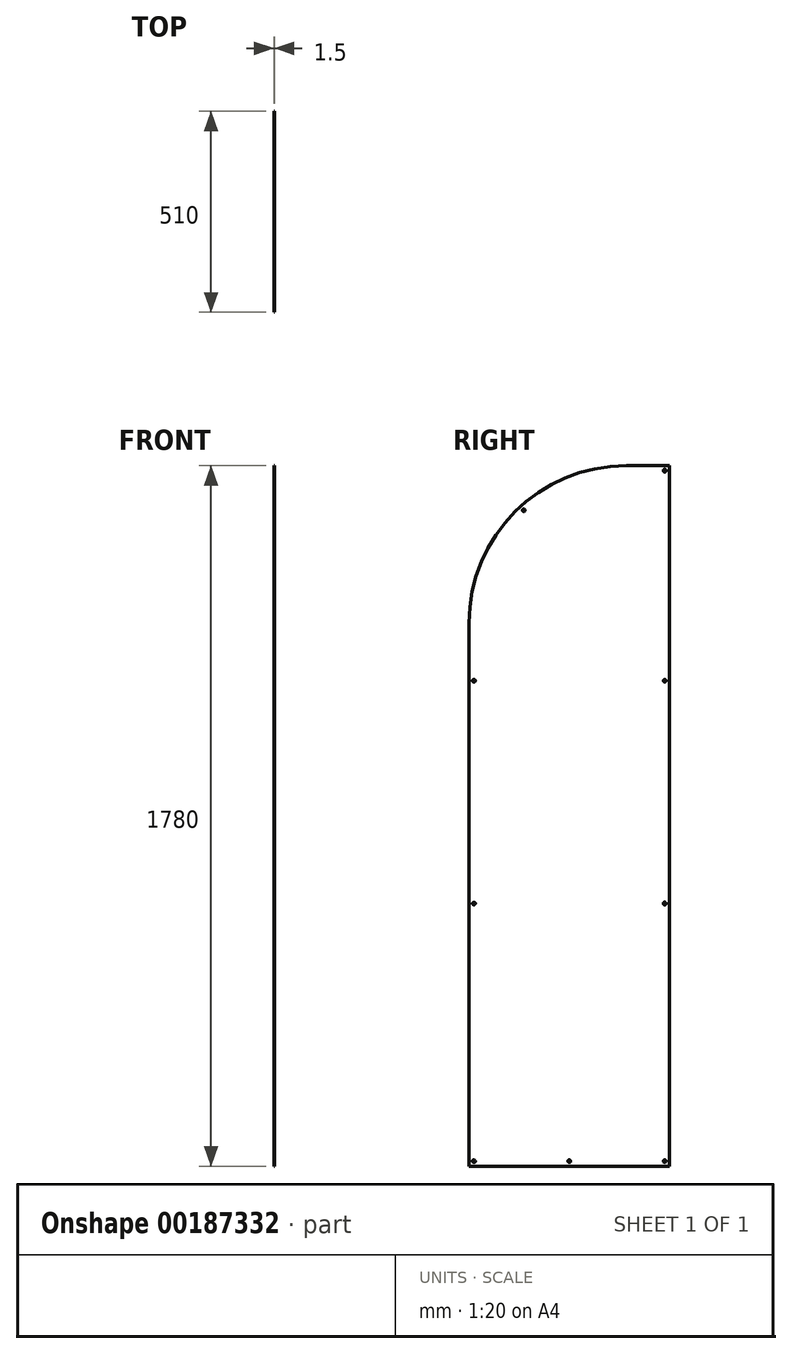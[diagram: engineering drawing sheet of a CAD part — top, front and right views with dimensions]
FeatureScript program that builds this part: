
annotation { "Feature Type Name" : "Feature", "Feature Type Description" : "" }
export const myFeature = defineFeature(function(context is Context, id is Id, definition is map)
    precondition{}
    {
        {
            var Q0;
            Q0=qCreatedBy(makeId("Right.planeOp"),FACE);
            var sketch = newSketch(context, id + "F0", { "sketchPlane" : qUnion([Q0])});
            skLineSegment(sketch, "E0.bottom", {"start": v(255, 890) * mm, "end": v(145, 890) * mm});
            skLineSegment(sketch, "E0.top", {"start": v(255, -890) * mm, "end": v(-255, -890) * mm});
            skLineSegment(sketch, "E0.left", {"start": v(255, 890) * mm, "end": v(255, -890) * mm});
            skLineSegment(sketch, "E0.right", {"start": v(-255, 490) * mm, "end": v(-255, -890) * mm});
            skPoint(sketch, "E0.middle", {"position": v(0, 0) * mm});
            skPoint(sketch, "E1.visualSharp", {"position": v(-255, 890) * mm});
            skArc(sketch, "E1.filletArc", {"start": v(145, 890) * mm, "mid": v(-137.84, 772.84) * mm, "end": v(-255, 490) * mm});
            skCircle(sketch, "E2", {"center": v(0, -877.3) * mm, "radius": 3.5 * mm});
            skCircle(sketch, "E3", {"center": v(-242.3, -877.3) * mm, "radius": 3.5 * mm});
            skCircle(sketch, "E4", {"center": v(242.3, -877.3) * mm, "radius": 3.5 * mm});
            skCircle(sketch, "E5", {"center": v(242.3, -222.65) * mm, "radius": 3.5 * mm});
            skCircle(sketch, "E6", {"center": v(-242.3, -222.65) * mm, "radius": 3.5 * mm});
            skCircle(sketch, "E7", {"center": v(242.3, 343.45) * mm, "radius": 3.5 * mm});
            skCircle(sketch, "E8", {"center": v(-242.3, 343.45) * mm, "radius": 3.5 * mm});
            skCircle(sketch, "E9", {"center": v(242.3, 877.3) * mm, "radius": 3.5 * mm});
            skCircle(sketch, "E10", {"center": v(-115.64, 776.47) * mm, "radius": 3.5 * mm});
            skSolve(sketch);
        }
        {
            var Q0;
            Q0=qSketchRegion(id+"F0",true);
            extrude(context, id + "F1", {"entities" : qUnion([Q0]), "endBound" : BoundingType.SYMMETRIC, "depth" : 1.5 * mm});
        }
    });
